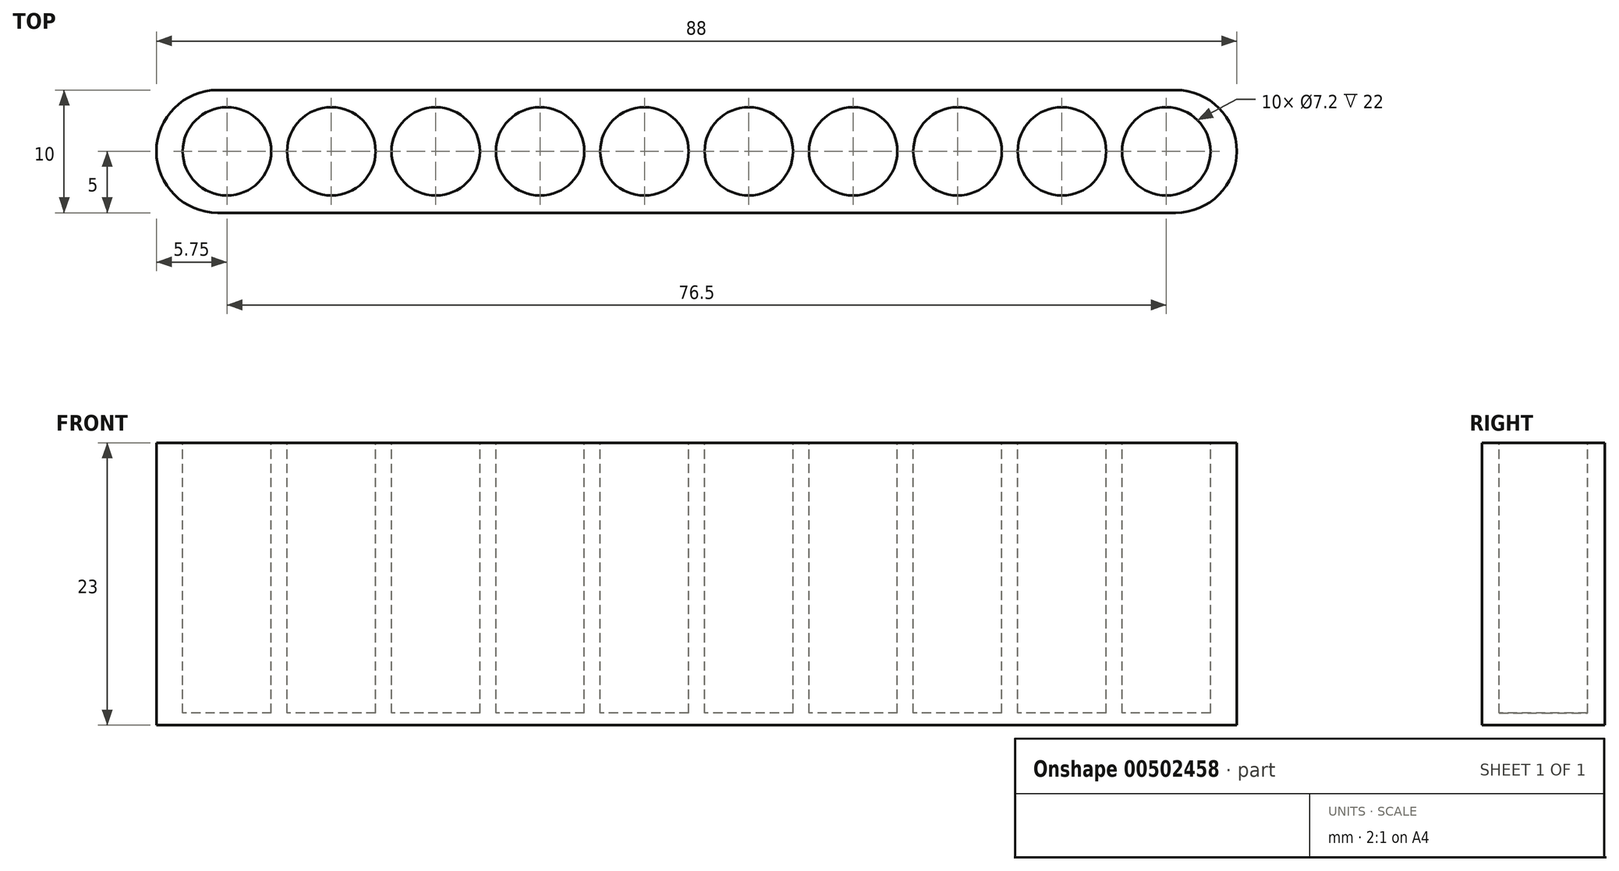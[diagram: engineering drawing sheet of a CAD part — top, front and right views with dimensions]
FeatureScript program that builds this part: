
annotation { "Feature Type Name" : "Feature", "Feature Type Description" : "" }
export const myFeature = defineFeature(function(context is Context, id is Id, definition is map)
    precondition{}
    {
        {
            var Q0;
            Q0=qCreatedBy(makeId("Top.planeOp"),FACE);
            var sketch = newSketch(context, id + "F0", { "sketchPlane" : qUnion([Q0])});
            skLineSegment(sketch, "E0.bottom", {"start": v(-44, 5) * mm, "end": v(44, 5) * mm});
            skLineSegment(sketch, "E0.top", {"start": v(-44, -5) * mm, "end": v(44, -5) * mm});
            skLineSegment(sketch, "E0.left", {"start": v(-44, 5) * mm, "end": v(-44, -5) * mm});
            skLineSegment(sketch, "E0.right", {"start": v(44, 5) * mm, "end": v(44, -5) * mm});
            skLineSegment(sketch, "E1", {"start": v(0, 39.5) * mm, "end": v(0, -26.18) * mm, "construction": true});
            skLineSegment(sketch, "E2", {"start": v(-38.73, 0) * mm, "end": v(38.14, 0) * mm, "construction": true});
            skSolve(sketch);
        }
        {
            var Q0;
            Q0=makeQuery(id+"F0.imprint","IMPRINT",FACE,{"disambiguationData":[TD([[makeQuery(id+"F0.imprint","IMPRINT",EDGE,{"derivedFrom":sQuery(id+"F0.wireOp",EDGE,"E0.bottom")}),-1.0]])]});
            extrude(context, id + "F1", {"entities" : qUnion([Q0]), "depth" : 23 * mm, "offsetDistance" : 25 * mm});
        }
        {
            var Q0;
            Q0=makeQuery(id+"F1.opExtrude","CAP_FACE",FACE,{"disambiguationData":[OSD([sQuery(id+"F0.wireOp",EDGE,"E0.bottom"),sQuery(id+"F0.wireOp",EDGE,"E0.top"),sQuery(id+"F0.wireOp",EDGE,"E0.left"),sQuery(id+"F0.wireOp",EDGE,"E0.right")])],"isStart":false});
            var sketch = newSketch(context, id + "F2", { "sketchPlane" : qUnion([Q0])});
            skCircle(sketch, "E3", {"center": v(-38.25, 0) * mm, "radius": 3.6 * mm});
            skCircle(sketch, "E4.1.0.0", {"center": v(-29.75, 0) * mm, "radius": 3.6 * mm});
            skCircle(sketch, "E4.2.0.0", {"center": v(-21.25, 0) * mm, "radius": 3.6 * mm});
            skCircle(sketch, "E4.3.0.0", {"center": v(-12.75, 0) * mm, "radius": 3.6 * mm});
            skCircle(sketch, "E4.4.0.0", {"center": v(-4.25, 0) * mm, "radius": 3.6 * mm});
            skCircle(sketch, "E4.5.0.0", {"center": v(4.25, 0) * mm, "radius": 3.6 * mm});
            skCircle(sketch, "E4.6.0.0", {"center": v(12.75, 0) * mm, "radius": 3.6 * mm});
            skCircle(sketch, "E4.7.0.0", {"center": v(21.25, 0) * mm, "radius": 3.6 * mm});
            skCircle(sketch, "E4.8.0.0", {"center": v(29.75, 0) * mm, "radius": 3.6 * mm});
            skCircle(sketch, "E4.9.0.0", {"center": v(38.25, 0) * mm, "radius": 3.6 * mm});
            skLineSegment(sketch, "E4.direction1", {"start": v(-38.25, 0) * mm, "end": v(-29.75, 0) * mm, "construction": true});
            skSolve(sketch);
        }
        {
            var Q0;
            Q0=makeQuery(id+"F2.imprint","IMPRINT",FACE,{"disambiguationData":[TD([[makeQuery(id+"F2.imprint","IMPRINT",EDGE,{"derivedFrom":sQuery(id+"F2.wireOp",EDGE,"E3")}),1.0]])]});
            var Q1;
            Q1=makeQuery(id+"F2.imprint","IMPRINT",FACE,{"disambiguationData":[TD([[makeQuery(id+"F2.imprint","IMPRINT",EDGE,{"derivedFrom":sQuery(id+"F2.wireOp",EDGE,"E4.1.0.0")}),1.0]])]});
            var Q2;
            Q2=makeQuery(id+"F2.imprint","IMPRINT",FACE,{"disambiguationData":[TD([[makeQuery(id+"F2.imprint","IMPRINT",EDGE,{"derivedFrom":sQuery(id+"F2.wireOp",EDGE,"E4.2.0.0")}),1.0]])]});
            var Q3;
            Q3=makeQuery(id+"F2.imprint","IMPRINT",FACE,{"disambiguationData":[TD([[makeQuery(id+"F2.imprint","IMPRINT",EDGE,{"derivedFrom":sQuery(id+"F2.wireOp",EDGE,"E4.3.0.0")}),1.0]])]});
            var Q4;
            Q4=makeQuery(id+"F2.imprint","IMPRINT",FACE,{"disambiguationData":[TD([[makeQuery(id+"F2.imprint","IMPRINT",EDGE,{"derivedFrom":sQuery(id+"F2.wireOp",EDGE,"E4.4.0.0")}),1.0]])]});
            var Q5;
            Q5=makeQuery(id+"F2.imprint","IMPRINT",FACE,{"disambiguationData":[TD([[makeQuery(id+"F2.imprint","IMPRINT",EDGE,{"derivedFrom":sQuery(id+"F2.wireOp",EDGE,"E4.5.0.0")}),1.0]])]});
            var Q6;
            Q6=makeQuery(id+"F2.imprint","IMPRINT",FACE,{"disambiguationData":[TD([[makeQuery(id+"F2.imprint","IMPRINT",EDGE,{"derivedFrom":sQuery(id+"F2.wireOp",EDGE,"E4.6.0.0")}),1.0]])]});
            var Q7;
            Q7=makeQuery(id+"F2.imprint","IMPRINT",FACE,{"disambiguationData":[TD([[makeQuery(id+"F2.imprint","IMPRINT",EDGE,{"derivedFrom":sQuery(id+"F2.wireOp",EDGE,"E4.7.0.0")}),1.0]])]});
            var Q8;
            Q8=makeQuery(id+"F2.imprint","IMPRINT",FACE,{"disambiguationData":[TD([[makeQuery(id+"F2.imprint","IMPRINT",EDGE,{"derivedFrom":sQuery(id+"F2.wireOp",EDGE,"E4.8.0.0")}),1.0]])]});
            var Q9;
            Q9=makeQuery(id+"F2.imprint","IMPRINT",FACE,{"disambiguationData":[TD([[makeQuery(id+"F2.imprint","IMPRINT",EDGE,{"derivedFrom":sQuery(id+"F2.wireOp",EDGE,"E4.9.0.0")}),1.0]])]});
            extrude(context, id + "F3", {"entities" : qUnion([Q0, Q1, Q2, Q3, Q4, Q5, Q6, Q7, Q8, Q9]), "operationType" : NewBodyOperationType.REMOVE, "oppositeDirection" : true, "depth" : 22 * mm, "offsetDistance" : 25 * mm});
        }
        {
            var Q0;
            Q0=makeQuery(id+"F1.opExtrude","SWEPT_EDGE",EDGE,{"disambiguationData":[OSD([sQuery(id+"F0.wireOp",EDGE,"E0.bottom"),sQuery(id+"F0.wireOp",EDGE,"E0.right")])]});
            var Q1;
            Q1=makeQuery(id+"F1.opExtrude","SWEPT_EDGE",EDGE,{"disambiguationData":[OSD([sQuery(id+"F0.wireOp",EDGE,"E0.top"),sQuery(id+"F0.wireOp",EDGE,"E0.right")])]});
            var Q2;
            Q2=makeQuery(id+"F1.opExtrude","SWEPT_EDGE",EDGE,{"disambiguationData":[OSD([sQuery(id+"F0.wireOp",EDGE,"E0.top"),sQuery(id+"F0.wireOp",EDGE,"E0.left")])]});
            var Q3;
            Q3=makeQuery(id+"F1.opExtrude","SWEPT_EDGE",EDGE,{"disambiguationData":[OSD([sQuery(id+"F0.wireOp",EDGE,"E0.bottom"),sQuery(id+"F0.wireOp",EDGE,"E0.left")])]});
            fillet(context, id + "F4", {"entities" : qUnion([Q0, Q1, Q2, Q3]), "radius" : 5 * mm, "tangentPropagation" : true, "allowEdgeOverflow" : false});
        }
    });
